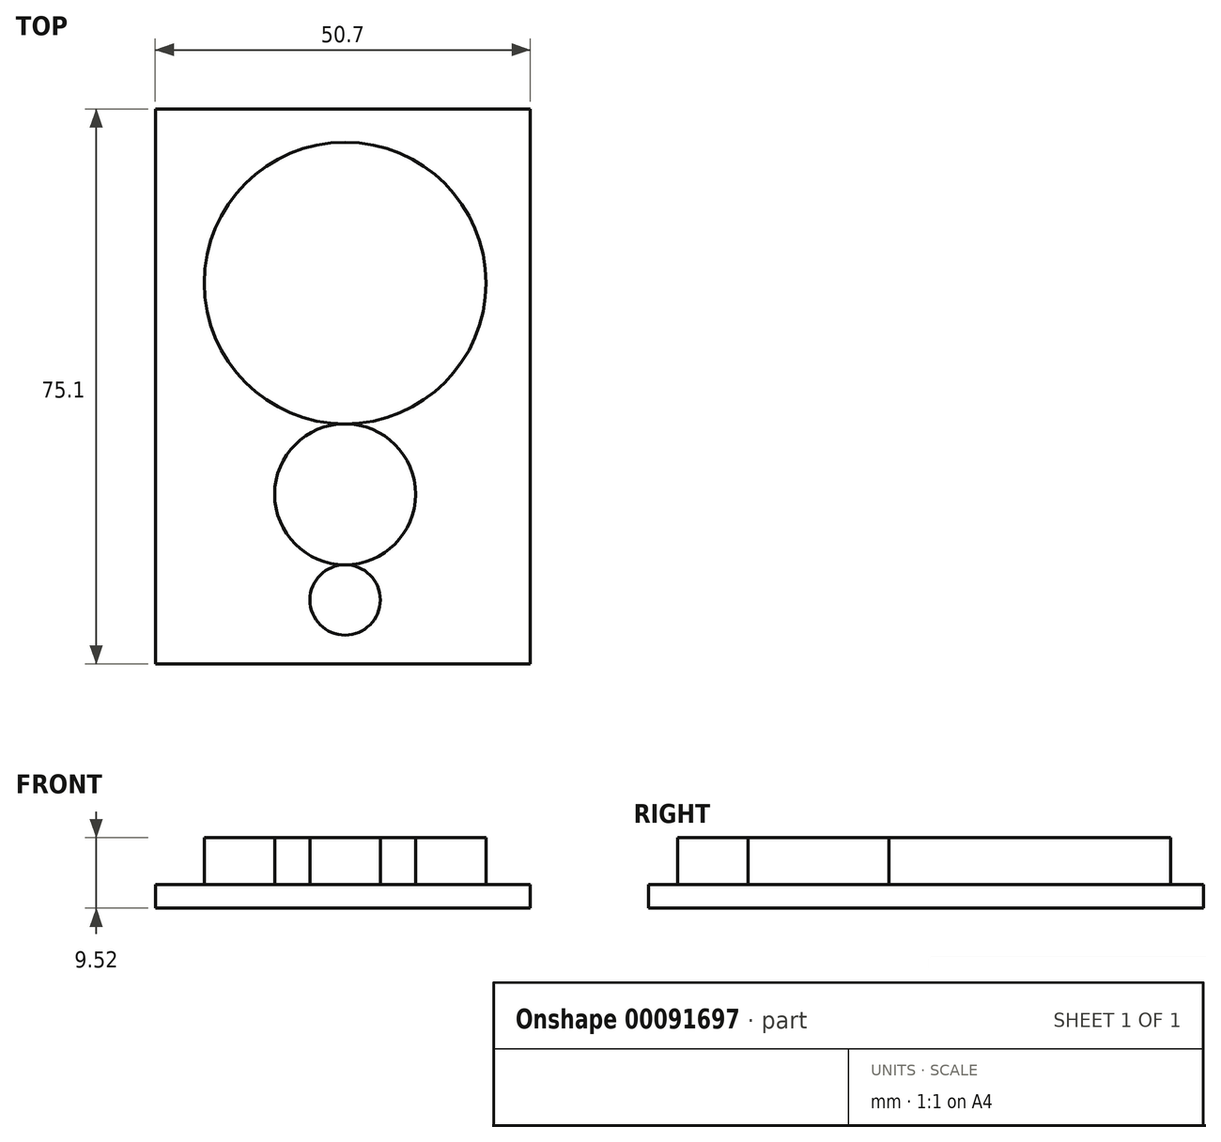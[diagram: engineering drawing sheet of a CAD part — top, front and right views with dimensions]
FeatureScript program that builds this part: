
annotation { "Feature Type Name" : "Feature", "Feature Type Description" : "" }
export const myFeature = defineFeature(function(context is Context, id is Id, definition is map)
    precondition{}
    {
        {
            var Q0;
            Q0=qCreatedBy(makeId("Top.planeOp"),FACE);
            var sketch = newSketch(context, id + "F0", { "sketchPlane" : qUnion([Q0])});
            skCircle(sketch, "E0", {"center": v(0, 0) * mm, "radius": 9.53 * mm});
            skCircle(sketch, "E1", {"center": v(0, 28.58) * mm, "radius": 19.05 * mm});
            skCircle(sketch, "E2", {"center": v(0, -14.29) * mm, "radius": 4.76 * mm});
            skLineSegment(sketch, "E3.bottom", {"start": v(-25.67, 52.13) * mm, "end": v(25.03, 52.13) * mm});
            skLineSegment(sketch, "E3.top", {"start": v(-25.67, -22.97) * mm, "end": v(25.03, -22.97) * mm});
            skLineSegment(sketch, "E3.left", {"start": v(-25.67, 52.13) * mm, "end": v(-25.67, -22.97) * mm});
            skLineSegment(sketch, "E3.right", {"start": v(25.03, 52.13) * mm, "end": v(25.03, -22.97) * mm});
            skSolve(sketch);
        }
        {
            var Q0;
            Q0=makeQuery(id+"F0.imprint","IMPRINT",FACE,{"disambiguationData":[TD([[makeQuery(id+"F0.imprint","IMPRINT",EDGE,{"derivedFrom":sQuery(id+"F0.wireOp",EDGE,"E1")}),1.0]])]});
            extrude(context, id + "F1", {"entities" : qUnion([Q0]), "depth" : 6.35 * mm});
        }
        {
            var Q0;
            {var subQ0=sQuery(id+"F0.wireOp",EDGE,"E0");var subQ1=makeQuery(id+"F0.imprint","INTERSECT",VERTEX,{"derivedFrom":[subQ0,sQuery(id+"F0.wireOp",EDGE,"E1")]});Q0=makeQuery(id+"F0.imprint","IMPRINT",FACE,{"disambiguationData":[TD([[makeQuery(id+"F0.imprint","IMPRINT",EDGE,{"disambiguationData":[TD([[subQ1,-1.0]])],"derivedFrom":subQ0}),1.0]])]});}
            extrude(context, id + "F2", {"entities" : qUnion([Q0]), "depth" : 6.35 * mm});
        }
        {
            var Q0;
            Q0=makeQuery(id+"F0.imprint","IMPRINT",FACE,{"disambiguationData":[TD([[makeQuery(id+"F0.imprint","IMPRINT",EDGE,{"derivedFrom":sQuery(id+"F0.wireOp",EDGE,"E2")}),1.0]])]});
            extrude(context, id + "F3", {"entities" : qUnion([Q0]), "depth" : 6.35 * mm});
        }
        {
            var Q0;
            {var subQ1=sQuery(id+"F0.wireOp",EDGE,"E1");Q0=makeQuery(id+"F0.imprint","IMPRINT",FACE,{"disambiguationData":[TD([[makeQuery(id+"F0.imprint","IMPRINT",EDGE,{"derivedFrom":subQ1}),-1.0]])]});}
            var Q1;
            Q1=makeQuery(id+"F0.imprint","IMPRINT",FACE,{"disambiguationData":[TD([[makeQuery(id+"F0.imprint","IMPRINT",EDGE,{"derivedFrom":sQuery(id+"F0.wireOp",EDGE,"E1")}),1.0]])]});
            var Q2;
            {var subQ0=sQuery(id+"F0.wireOp",EDGE,"E0");var subQ1=makeQuery(id+"F0.imprint","INTERSECT",VERTEX,{"derivedFrom":[subQ0,sQuery(id+"F0.wireOp",EDGE,"E1")]});Q2=makeQuery(id+"F0.imprint","IMPRINT",FACE,{"disambiguationData":[TD([[makeQuery(id+"F0.imprint","IMPRINT",EDGE,{"disambiguationData":[TD([[subQ1,-1.0]])],"derivedFrom":subQ0}),1.0]])]});}
            var Q3;
            Q3=makeQuery(id+"F0.imprint","IMPRINT",FACE,{"disambiguationData":[TD([[makeQuery(id+"F0.imprint","IMPRINT",EDGE,{"derivedFrom":sQuery(id+"F0.wireOp",EDGE,"E2")}),1.0]])]});
            extrude(context, id + "F4", {"entities" : qUnion([Q0, Q1, Q2, Q3]), "oppositeDirection" : true, "depth" : 3.17 * mm});
        }
    });
